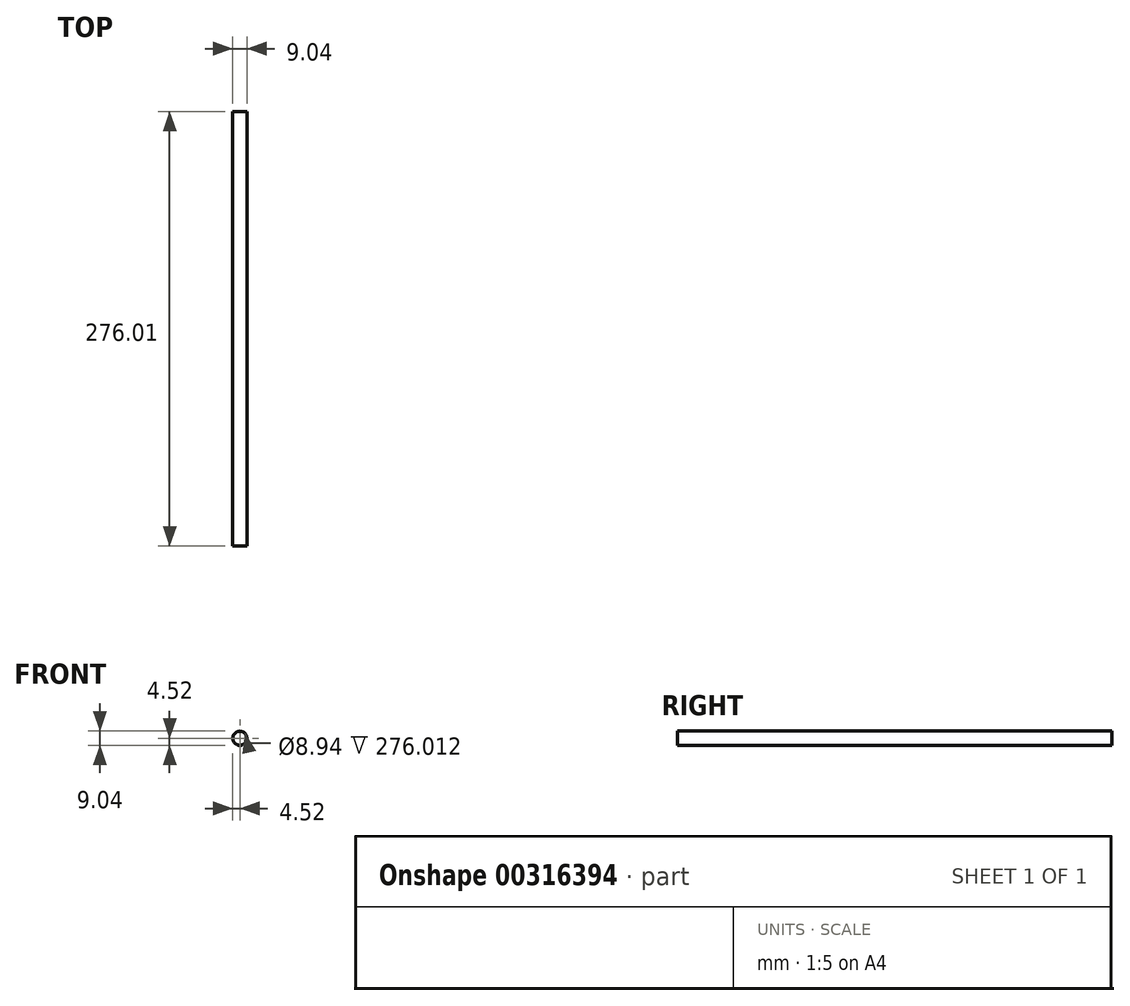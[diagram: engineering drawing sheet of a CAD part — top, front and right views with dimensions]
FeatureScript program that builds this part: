
annotation { "Feature Type Name" : "Feature", "Feature Type Description" : "" }
export const myFeature = defineFeature(function(context is Context, id is Id, definition is map)
    precondition{}
    {
        {
            var Q0;
            Q0=qCreatedBy(makeId("Front.planeOp"),FACE);
            cPlane(context, id + "F0", {"entities" : qUnion([Q0]), "cplaneType" : CPlaneType.OFFSET, "offset" : 276 * mm, "oppositeDirection" : true, "width" : 152.4 * mm, "height" : 152.4 * mm});
        }
        {
            var Q0;
            Q0=qCreatedBy(makeId("Top.planeOp"),FACE);
            cPlane(context, id + "F1", {"entities" : qUnion([Q0]), "cplaneType" : CPlaneType.OFFSET, "offset" : 4.52 * mm, "width" : 152.4 * mm, "height" : 152.4 * mm});
        }
        {
            var Q0;
            Q0=qCreatedBy(id+"F1.planeOp",FACE);
            cPlane(context, id + "F2", {"entities" : qUnion([Q0]), "cplaneType" : CPlaneType.OFFSET, "offset" : 0.04 * mm, "oppositeDirection" : true, "width" : 152.4 * mm, "height" : 152.4 * mm});
        }
        {
            var Q0;
            Q0=qCreatedBy(makeId("Right.planeOp"),FACE);
            var sketch = newSketch(context, id + "F3", { "sketchPlane" : qUnion([Q0])});
            skLineSegment(sketch, "E0.bottom", {"start": v(0, 4.47) * mm, "end": v(276.01, 4.47) * mm});
            skLineSegment(sketch, "E0.top", {"start": v(0, 4.52) * mm, "end": v(276.01, 4.52) * mm});
            skLineSegment(sketch, "E0.left", {"start": v(0, 4.52) * mm, "end": v(0, 4.47) * mm});
            skLineSegment(sketch, "E0.right", {"start": v(276.01, 4.52) * mm, "end": v(276.01, 4.47) * mm});
            skLineSegment(sketch, "E1", {"start": v(0, 0) * mm, "end": v(17.58, 0) * mm, "construction": true});
            skSolve(sketch);
        }
        {
            var Q0;
            Q0 = qSketchRegion(id + "F3", true);
            var Q1;
            Q1=sQuery(id+"F3.wireOp",EDGE,"E1");
            revolve(context, id + "F4", {"entities" : qUnion([Q0]), "axis" : qUnion([Q1]), "revolveType" : RevolveType.FULL});
        }
    });
